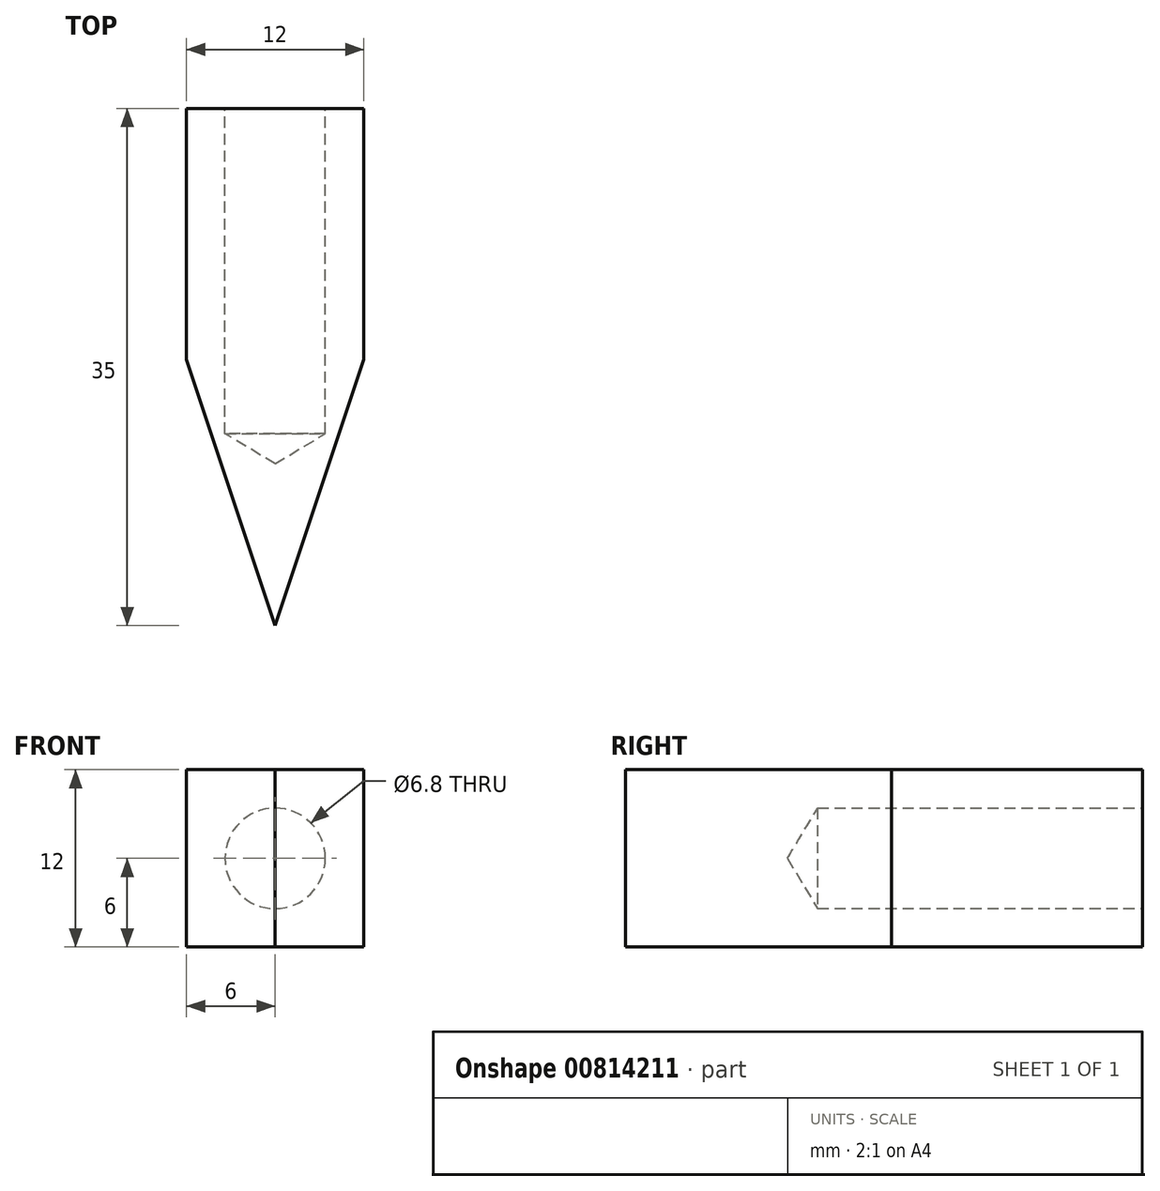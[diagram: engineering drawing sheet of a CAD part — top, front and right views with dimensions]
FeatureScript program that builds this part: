
annotation { "Feature Type Name" : "Feature", "Feature Type Description" : "" }
export const myFeature = defineFeature(function(context is Context, id is Id, definition is map)
    precondition{}
    {
        {
            var Q0;
            Q0=qCreatedBy(makeId("Front.planeOp"),FACE);
            var sketch = newSketch(context, id + "F0", { "sketchPlane" : qUnion([Q0])});
            skLineSegment(sketch, "E0.bottom", {"start": v(6, -6) * mm, "end": v(-6, -6) * mm});
            skLineSegment(sketch, "E0.top", {"start": v(6, 6) * mm, "end": v(-6, 6) * mm});
            skLineSegment(sketch, "E0.left", {"start": v(6, -6) * mm, "end": v(6, 6) * mm});
            skLineSegment(sketch, "E0.right", {"start": v(-6, -6) * mm, "end": v(-6, 6) * mm});
            skPoint(sketch, "E0.middle", {"position": v(0, 0) * mm});
            skSolve(sketch);
        }
        {
            var Q0;
            Q0=makeQuery(id+"F0.imprint","IMPRINT",FACE,{"disambiguationData":[TD([[makeQuery(id+"F0.imprint","IMPRINT",EDGE,{"derivedFrom":sQuery(id+"F0.wireOp",EDGE,"E0.bottom")}),-1.0]])]});
            extrude(context, id + "F1", {"entities" : qUnion([Q0]), "depth" : 35 * mm, "offsetDistance" : 25 * mm});
        }
        {
            var Q0;
            Q0=makeQuery(id+"F1.opExtrude","SWEPT_FACE",FACE,{"disambiguationData":[OSD([sQuery(id+"F0.wireOp",EDGE,"E0.top")])]});
            var sketch = newSketch(context, id + "F2", { "sketchPlane" : qUnion([Q0])});
            skPoint(sketch, "E1", {"position": v(-6, -17) * mm});
            skPoint(sketch, "E2", {"position": v(6, -17) * mm});
            skLineSegment(sketch, "E3", {"start": v(0, -35) * mm, "end": v(-6, -17) * mm});
            skLineSegment(sketch, "E4", {"start": v(0, -35) * mm, "end": v(6, -17) * mm});
            skSolve(sketch);
        }
        {
            var Q0;
            Q0 = qSketchRegion(id + "F2", true);
            var Q1;
            {var subQ0=sQuery(id+"F2.wireOp",EDGE,"E3");Q1=makeQuery(id+"F2.imprint","IMPRINT",FACE,{"disambiguationData":[TD([[makeQuery(id+"F2.imprint","IMPRINT",EDGE,{"derivedFrom":subQ0}),1.0]])]});}
            var Q2;
            {var subQ0=sQuery(id+"F2.wireOp",EDGE,"E4");Q2=makeQuery(id+"F2.imprint","IMPRINT",FACE,{"disambiguationData":[TD([[makeQuery(id+"F2.imprint","IMPRINT",EDGE,{"derivedFrom":subQ0}),-1.0]])]});}
            extrude(context, id + "F3", {"entities" : qUnion([Q0, Q1, Q2]), "operationType" : NewBodyOperationType.REMOVE, "oppositeDirection" : true, "depth" : 25 * mm, "offsetDistance" : 25 * mm});
        }
        {
            var Q0;
            Q0=makeQuery(id+"F1.opExtrude","CAP_FACE",FACE,{"disambiguationData":[OSD([sQuery(id+"F0.wireOp",EDGE,"E0.bottom"),sQuery(id+"F0.wireOp",EDGE,"E0.top"),sQuery(id+"F0.wireOp",EDGE,"E0.left"),sQuery(id+"F0.wireOp",EDGE,"E0.right")])],"isStart":true});
            var sketch = newSketch(context, id + "F4", { "sketchPlane" : qUnion([Q0])});
            skPoint(sketch, "E5", {"position": v(0, 0) * mm});
            skSolve(sketch);
        }
        {
            var Q0;
            Q0=sQuery(id+"F4.wireOp",VERTEX,"E5");
            var Q1;
            Q1=makeQuery(id+"F1.opExtrude","SWEPT_BODY",BODY,{"disambiguationData":[OSD([sQuery(id+"F0.wireOp",EDGE,"E0.bottom"),sQuery(id+"F0.wireOp",EDGE,"E0.top"),sQuery(id+"F0.wireOp",EDGE,"E0.left"),sQuery(id+"F0.wireOp",EDGE,"E0.right")])]});
            hole(context, id + "F5", {"style" : HoleStyle.SIMPLE, "endStyle" : HoleEndStyle.BLIND, "standardTappedOrClearance" : lookupTablePath({ "standard" : "ISO", "engagement" : "75%", "pitch" : "1.25 mm", "size" : "M8", "type" : "Tapped" }), "standardBlindInLast" : lookupTablePath({ "standard" : "ISO", "engagement" : "75%", "pitch" : "1.25 mm", "size" : "M8", "type" : "Tapped" }), "holeDiameter" : 6.8 * mm, "majorDiameter" : 8 * mm, "showTappedDepth" : true, "holeDepth" : 22 * mm, "isTappedThrough" : true, "tappedDepth" : 18.25 * mm, "tapClearance" : 3, "locations" : qUnion([Q0]), "scope" : qUnion([Q1])});
        }
    });
